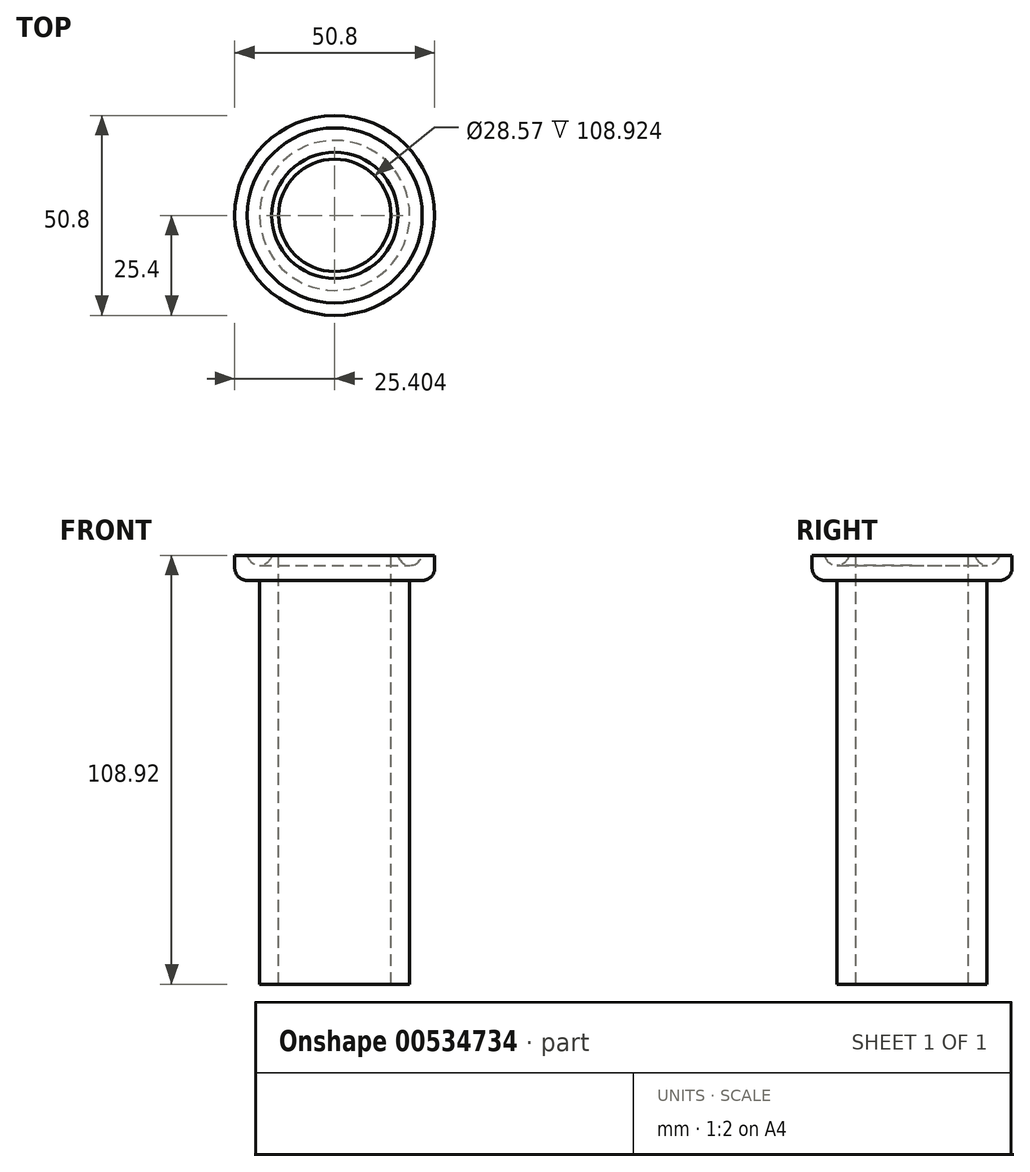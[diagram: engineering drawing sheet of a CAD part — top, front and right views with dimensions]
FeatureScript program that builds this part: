
annotation { "Feature Type Name" : "Feature", "Feature Type Description" : "" }
export const myFeature = defineFeature(function(context is Context, id is Id, definition is map)
    precondition{}
    {
        {
            var Q0;
            Q0=qCreatedBy(makeId("Front.planeOp"),FACE);
            var sketch = newSketch(context, id + "F0", { "sketchPlane" : qUnion([Q0])});
            skLineSegment(sketch, "E0.left", {"start": v(-88.73, 1.9) * mm, "end": v(-88.73, -1.27) * mm});
            skLineSegment(sketch, "E1.left", {"start": v(-82.38, -4.45) * mm, "end": v(-82.38, -107.02) * mm});
            skPoint(sketch, "E2.visualSharp", {"position": v(-88.73, -4.45) * mm});
            skArc(sketch, "E2.filletArc", {"start": v(-88.73, -1.27) * mm, "mid": v(-87.8, -3.52) * mm, "end": v(-85.55, -4.45) * mm});
            skArc(sketch, "E3", {"start": v(-85.55, 1.9) * mm, "mid": v(-82.44, -0.61) * mm, "end": v(-79.34, 1.9) * mm});
            skLineSegment(sketch, "E4", {"start": v(-85.55, -4.45) * mm, "end": v(-82.38, -4.45) * mm});
            skLineSegment(sketch, "E5", {"start": v(-88.73, 1.9) * mm, "end": v(-85.55, 1.9) * mm});
            skLineSegment(sketch, "E6", {"start": v(-63.33, 24.07) * mm, "end": v(-63.33, -133.6) * mm, "construction": true});
            skLineSegment(sketch, "E7", {"start": v(-79.34, 1.9) * mm, "end": v(-63.33, 1.9) * mm});
            skLineSegment(sketch, "E8", {"start": v(-82.38, -107.02) * mm, "end": v(-63.33, -107.02) * mm});
            skLineSegment(sketch, "E9", {"start": v(-63.33, -107.02) * mm, "end": v(-63.33, 1.9) * mm});
            skSolve(sketch);
        }
        {
            var Q0;
            Q0 = qSketchRegion(id + "F0", true);
            var Q1;
            Q1=sQuery(id+"F0.wireOp",EDGE,"E6");
            revolve(context, id + "F1", {"entities" : qUnion([Q0]), "axis" : qUnion([Q1]), "revolveType" : RevolveType.FULL});
        }
        {
            var Q0;
            Q0=makeQuery(id+"F1.opRevolve","SWEPT_FACE",FACE,{"disambiguationData":[OSD([sQuery(id+"F0.wireOp",EDGE,"E7")])]});
            var sketch = newSketch(context, id + "F2", { "sketchPlane" : qUnion([Q0])});
            skPoint(sketch, "E10", {"position": v(-63.33, 0) * mm});
            skSolve(sketch);
        }
        {
            var Q0;
            Q0=sQuery(id+"F2.wireOp",VERTEX,"E10");
            var Q1;
            Q1=makeQuery(id+"F1.opRevolve","SWEPT_BODY",BODY,{"disambiguationData":[OSD([sQuery(id+"F0.wireOp",EDGE,"E0.left"),sQuery(id+"F0.wireOp",EDGE,"E1.left"),sQuery(id+"F0.wireOp",EDGE,"E2.filletArc"),sQuery(id+"F0.wireOp",EDGE,"E3"),sQuery(id+"F0.wireOp",EDGE,"E4"),sQuery(id+"F0.wireOp",EDGE,"E5"),sQuery(id+"F0.wireOp",EDGE,"E7"),sQuery(id+"F0.wireOp",EDGE,"E8"),sQuery(id+"F0.wireOp",EDGE,"E9")])]});
            hole(context, id + "F3", {"style" : HoleStyle.SIMPLE, "endStyle" : HoleEndStyle.THROUGH, "holeDiameter" : 28.57 * mm, "isTappedThrough" : true, "tappedDepth" : 12.7 * mm, "tapClearance" : 3, "locations" : qUnion([Q0]), "scope" : qUnion([Q1])});
        }
    });
